# Revit family: EKF_EE_ВертикальныйП-профиль(2шт)Trivia_AVERES
name_source: partatom
category: Электрооборудование
units: mm (PartAtom-declared; Revit-internal decimal feet)

## family parameters
Всегда вертикально = Нет
На основе рабочей плоскости = Да
Общий = Да
При загрузке вырезать с полостями = Нет
Размер круглого соединителя = Использовать диаметр
Тип детали = Силовой щит
Точка расчета площади = Нет

## types (2) — shared parameters
ADSK_Единица измерения = шт.
ADSK_Завод-изготовитель = EKF
ADSK_Количество = 1
ADSK_Материал = RAL 7035_Сталь
ADSK_Размер_Глубина = 42 мм
ADSK_Размер_Ширина = 23 мм
Изготовитель = EKF
Отметка по умолчанию = 1219.2 мм
Серия номенклатуры = Averes
Степень защиты IP = -
ТВ = EKF_2_TRIVIA_AVERES
Тип установки = -
zero-valued in all types: ADSK_Масса

## per-type parameters (varying)
| type | ADSK_Код изделия | ADSK_Марка | ADSK_Наименование | ADSK_Обозначение | ADSK_Размер_Высота | Тип |
| Вертикальный П-профиль В1900 (2шт) EKF AVERES | AVP19 | Вертикальный П-профиль В1900 (2 шт) EKF AVERES | Вертикальный П-профиль В1900 (2 шт) EKF AVERES | Вертикальный П-профиль В1900 (2 шт) EKF AVERES | 1924 мм | 644 мм |
| Вертикальный П-профиль В1700 (2шт) EKF AVERES | AVP17 | Вертикальный П-профиль В1700 (2 шт) EKF AVERES | Вертикальный П-профиль В1700 (2 шт) EKF AVERES | Вертикальный П-профиль В1700 (2 шт) EKF AVERES | 1650 мм | 643 мм |
